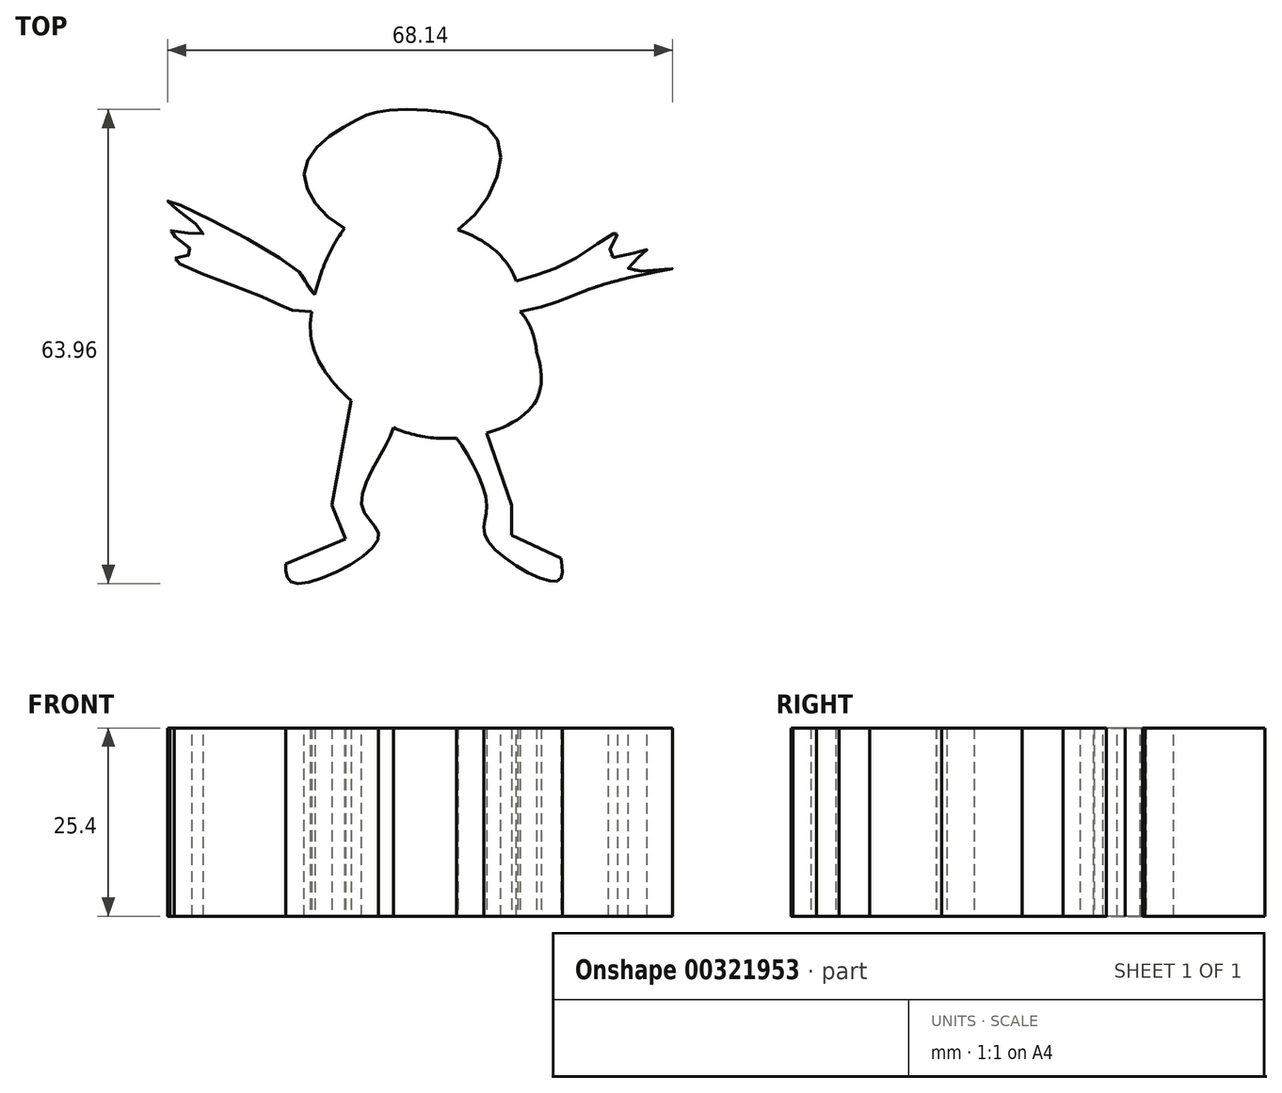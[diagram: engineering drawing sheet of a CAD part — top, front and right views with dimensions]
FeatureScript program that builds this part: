
annotation { "Feature Type Name" : "Feature", "Feature Type Description" : "" }
export const myFeature = defineFeature(function(context is Context, id is Id, definition is map)
    precondition{}
    {
        {
            var Q0;
            Q0=qCreatedBy(makeId("Top.planeOp"),FACE);
            var sketch = newSketch(context, id + "F0", { "sketchPlane" : qUnion([Q0])});
            skFitSpline(sketch, "E0", {"points": [v(15.75, 45.7) * mm, v(22.5, 51.89) * mm, v(27.56, 53.3) * mm, v(41.34, 49.92) * mm, v(36.35, 37.15) * mm, v(21.05, 37.3) * mm, v(15.75, 45.7) * mm]});
            skFitSpline(sketch, "E1", {"points": [v(21.05, 37.3) * mm, v(16.6, 26.12) * mm, v(18.02, 18.66) * mm, v(31.34, 9.3) * mm, v(46.97, 14.22) * mm, v(44.72, 26.1) * mm, v(36.35, 37.15) * mm], "startDerivative": vector(-44.16, -55.95) * mm, "endDerivative": vector(-88.11, 62.65) * mm});
            skLineSegment(sketch, "E2", {"start": v(21.93, 14.1) * mm, "end": v(19.3, 0) * mm});
            skLineSegment(sketch, "E3", {"start": v(19.3, 0) * mm, "end": v(21.2, -4.56) * mm});
            skLineSegment(sketch, "E4", {"start": v(21.2, -4.56) * mm, "end": v(13.1, -7.92) * mm});
            skLineSegment(sketch, "E5", {"start": v(40.25, 9.71) * mm, "end": v(43.62, 0) * mm});
            skLineSegment(sketch, "E6", {"start": v(43.62, 0) * mm, "end": v(43.62, -4.1) * mm});
            skLineSegment(sketch, "E7", {"start": v(43.62, -4.1) * mm, "end": v(50.23, -7.16) * mm});
            skFitSpline(sketch, "E8", {"points": [v(36.35, 37.15) * mm, v(42.2, 33.53) * mm, v(44.72, 27.98) * mm], "startDerivative": vector(14.12, -4.89) * mm, "endDerivative": vector(1.78, -14.37) * mm});
            skFitSpline(sketch, "E9", {"points": [v(27.63, 10.44) * mm, v(23.34, 0) * mm, v(25.6, -4.56) * mm, v(14.34, -10.55) * mm, v(13.1, -7.92) * mm], "startDerivative": vector(-5.28, -23.77) * mm, "endDerivative": vector(-0.24, 20.75) * mm});
            skFitSpline(sketch, "E10", {"points": [v(36.16, 9.02) * mm, v(40.25, 0) * mm, v(40.25, -4.64) * mm, v(49.78, -10.26) * mm, v(50.23, -7.16) * mm], "startDerivative": vector(15.4, -19.8) * mm, "endDerivative": vector(-4.34, 22.9) * mm});
            skFitSpline(sketch, "E11", {"points": [v(16.6, 26.12) * mm, v(10.88, 27.72) * mm, v(-1.92, 33.22) * mm, v(0.48, 34.08) * mm, v(-2.5, 36.98) * mm, v(2, 36.67) * mm, v(-2.82, 40.98) * mm, v(14.52, 31.8) * mm, v(17.03, 28.38) * mm], "startDerivative": vector(-84.8, -1.36) * mm, "endDerivative": vector(52.95, -57.48) * mm});
            skFitSpline(sketch, "E12", {"points": [v(44.43, 30.3) * mm, v(52.6, 33.53) * mm, v(57.93, 36.7) * mm, v(56.8, 33.53) * mm, v(61.87, 34.45) * mm, v(59.34, 31.92) * mm, v(65.25, 31.92) * mm, v(57.93, 30.3) * mm, v(51.18, 27.98) * mm, v(44.72, 26.1) * mm], "startDerivative": vector(58.89, 15.98) * mm, "endDerivative": vector(-76.22, -14.82) * mm});
            skPoint(sketch, "E13.2.internal.orphan", {"position": v(44.72, 19.27) * mm});
            skPoint(sketch, "E13.startDerivative.orphan", {"position": v(42.2, 31.92) * mm});
            skFitSpline(sketch, "E14", {"points": [v(44.2, 30.23) * mm, v(44.43, 30.3) * mm], "startDerivative": vector(0.23, 0.07) * mm, "endDerivative": vector(0.23, 0.07) * mm});
            skFitSpline(sketch, "E15", {"points": [v(44.72, 26.1) * mm, v(46.97, 19.27) * mm, v(44.43, 14.22) * mm, v(40.25, 9.71) * mm], "startDerivative": vector(13.16, -12.74) * mm, "endDerivative": vector(-12.67, -12.17) * mm});
            skSolve(sketch);
        }
        {
            var Q0;
            Q0 = qSketchRegion(id + "F0", true);
            extrude(context, id + "F1", {"entities" : qUnion([Q0]), "depth" : 25.4 * mm});
        }
        {
            var Q0;
            Q0 = qSketchRegion(id + "F0", true);
            extrude(context, id + "F2", {"entities" : qUnion([Q0]), "depth" : 25.4 * mm});
        }
    });
